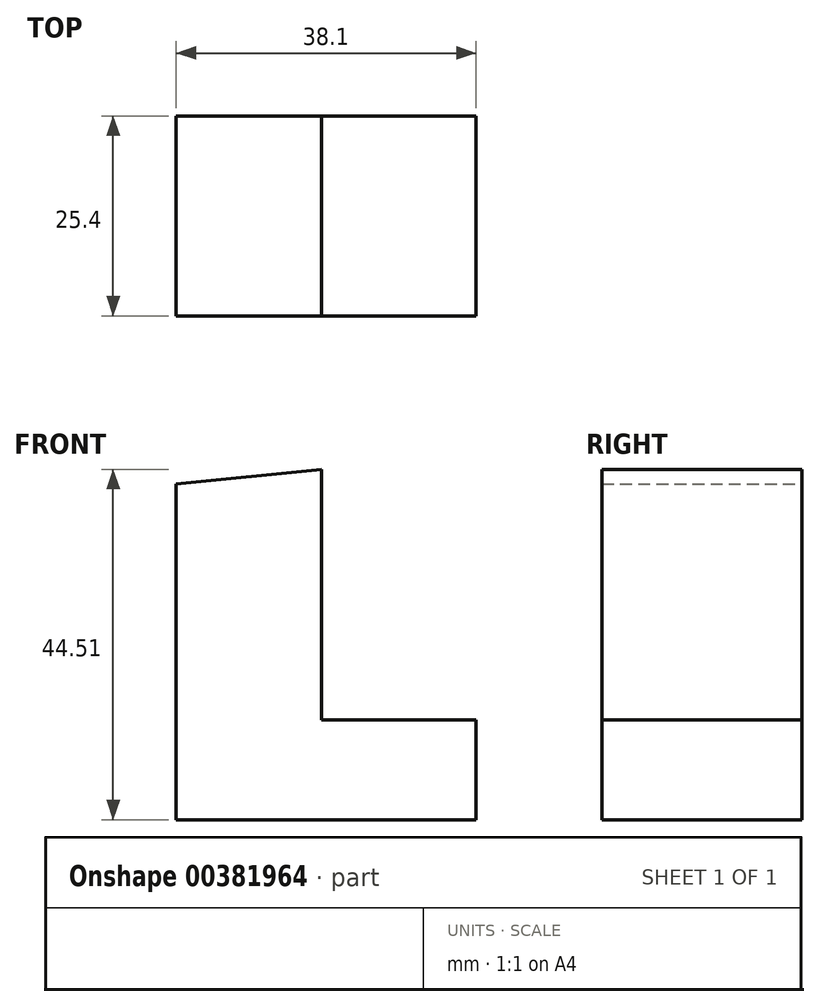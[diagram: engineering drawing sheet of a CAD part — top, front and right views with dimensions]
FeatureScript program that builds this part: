
annotation { "Feature Type Name" : "Feature", "Feature Type Description" : "" }
export const myFeature = defineFeature(function(context is Context, id is Id, definition is map)
    precondition{}
    {
        {
            var Q0;
            Q0=qCreatedBy(makeId("Front.planeOp"),FACE);
            var sketch = newSketch(context, id + "F0", { "sketchPlane" : qUnion([Q0])});
            skLineSegment(sketch, "E0", {"start": v(-82.24, 42.63) * mm, "end": v(-82.24, 0) * mm});
            skLineSegment(sketch, "E1", {"start": v(-82.24, 0) * mm, "end": v(-44.14, 0) * mm});
            skLineSegment(sketch, "E2", {"start": v(-44.14, 0) * mm, "end": v(-44.14, 12.7) * mm});
            skLineSegment(sketch, "E3", {"start": v(-44.14, 12.7) * mm, "end": v(-63.75, 12.7) * mm});
            skLineSegment(sketch, "E4", {"start": v(-63.75, 12.7) * mm, "end": v(-63.75, 44.51) * mm});
            skLineSegment(sketch, "E5", {"start": v(-63.75, 44.51) * mm, "end": v(-82.24, 42.63) * mm});
            skSolve(sketch);
        }
        {
            var Q0;
            Q0=makeQuery(id+"F0.imprint","IMPRINT",FACE,{"disambiguationData":[TD([[makeQuery(id+"F0.imprint","IMPRINT",EDGE,{"derivedFrom":sQuery(id+"F0.wireOp",EDGE,"E0")}),1.0]])]});
            extrude(context, id + "F1", {"entities" : qUnion([Q0]), "depth" : 25.4 * mm, "offsetDistance" : 25.4 * mm});
        }
    });
